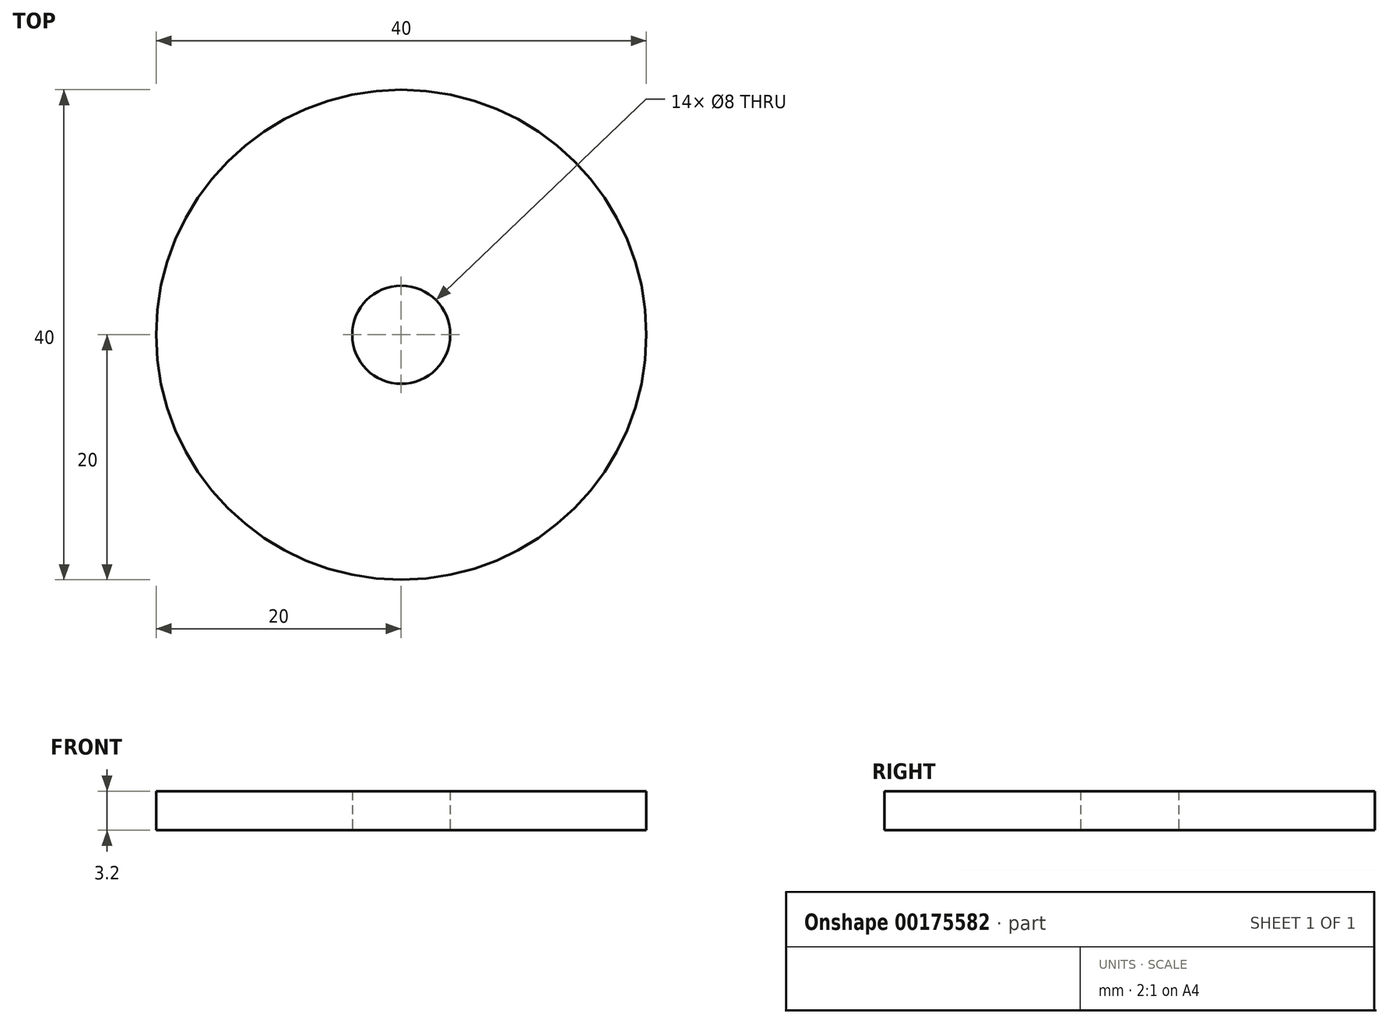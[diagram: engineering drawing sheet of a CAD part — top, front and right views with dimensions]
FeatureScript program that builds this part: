
annotation { "Feature Type Name" : "Feature", "Feature Type Description" : "" }
export const myFeature = defineFeature(function(context is Context, id is Id, definition is map)
    precondition{}
    {
        {
            var Q0;
            Q0=qCreatedBy(makeId("Top.planeOp"),FACE);
            var sketch = newSketch(context, id + "F0", { "sketchPlane" : qUnion([Q0])});
            skCircle(sketch, "E0", {"center": v(0, 0) * mm, "radius": 20 * mm});
            skCircle(sketch, "E1", {"center": v(0, 0) * mm, "radius": 4 * mm});
            skSolve(sketch);
        }
        {
            var Q0;
            Q0 = qSketchRegion(id + "F0", true);
            extrude(context, id + "F1", {"entities" : qUnion([Q0]), "depth" : 3.2 * mm});
        }
    });
